# Revit family: IS_TonicII_Multiproduct_BIM_DE_A6334;A6335
name_source: partatom
category: Plumbing Fixtures
revit_build: Autodesk Revit 2015 (Build: 20140606_1530(x64)
units: mm (PartAtom-declared; Revit-internal decimal feet)

## types (2) — shared parameters
AreaUnits = millimeters
Assembly Code = C1030200
AssetType = Fixed
Brand = Ideal Standard
ConnectionType = Plumbing
Default Elevation = 1219 mm
DurationUnit = year
ExpectedLife = 25
FaucetFunction = MIXED
FaucetOperation = Other
FaucetTopDescription = Lever
FaucetType = Other
Features = TONIC II build-in basin mixer
Finish = Chrome
IfcExportAs = IfcValveType
IfcExportType = FAUCET
InstallationDate = 1900-12-31T23:59:59
InstallationInstructions = www.idealstandard.de\produkte
LinearUnits = millimeters
ManufacturerURL = www.idealstandard.com
NBSDescription = Water supply fitting for wash basins and troughs
NBSReference = 45-35-70/371
NominalDepth = 241 mm
NominalHeight = 82 mm
NominalLength = 241 mm
NominalWidth = 193 mm  [stored 0.633202 ft]
ProductInformation = www.idealstandard.de/produkte
Shape = Sculptured
Size = 83 x 241 x 193 mm
Space = Internal
SpareParts = www.idealstandard.de/ersatzteile
TestPressure = 10 Bar
URL = www.idealstandard.com
Uniclass2015Code = Pr_40_20_87_98
Uniclass2015Title = Water supply fittings for wash basins and troughs
Uniclass2015Version = Products v1.1
Version = 1
VolumeUnits = Litres
WarrantyStartDate = 1900-12-31T23:59:59
WorkingPressure = 1-5 Bar

## per-type parameters (varying)
| type | A6334 | A6335 | BIMObjectName | BarCode | Description | ModelReference | Name | NettWeight |
| A6334AA | Yes | No | ISI_IdealStandard_WashBasinTaps_TonicII_A6334 | 4015413335010 | A6334AA TONIC II build-in basin mixer | Tonic ii single lever wall mounted basin mixer 255 mm spout | WashBasinTaps_TonicII_A6334_IdealStandard | 1.61 Kg |
| A6335AA | No | Yes | ISI_IdealStandard_WashBasinTaps_TonicII_A6335 | 4015413335034 | A6335AA TONIC II build-in basin mixer | Tonic ii single lever wall mounted basin mixer with 255 mm spout | WashBasinTaps_TonicII_A6335_IdealStandard | 1.78 Kg |

note: column(s) folded — value = type name in every type: Model, ModelNumber

note: [stored X ft] marks values corroborated as IEEE doubles in the binary element streams (Revit-internal decimal feet)

## geometry (parser evidence)
native form markers: Blend x2, Sweep x4
no freeform markers — native parametric forms only
